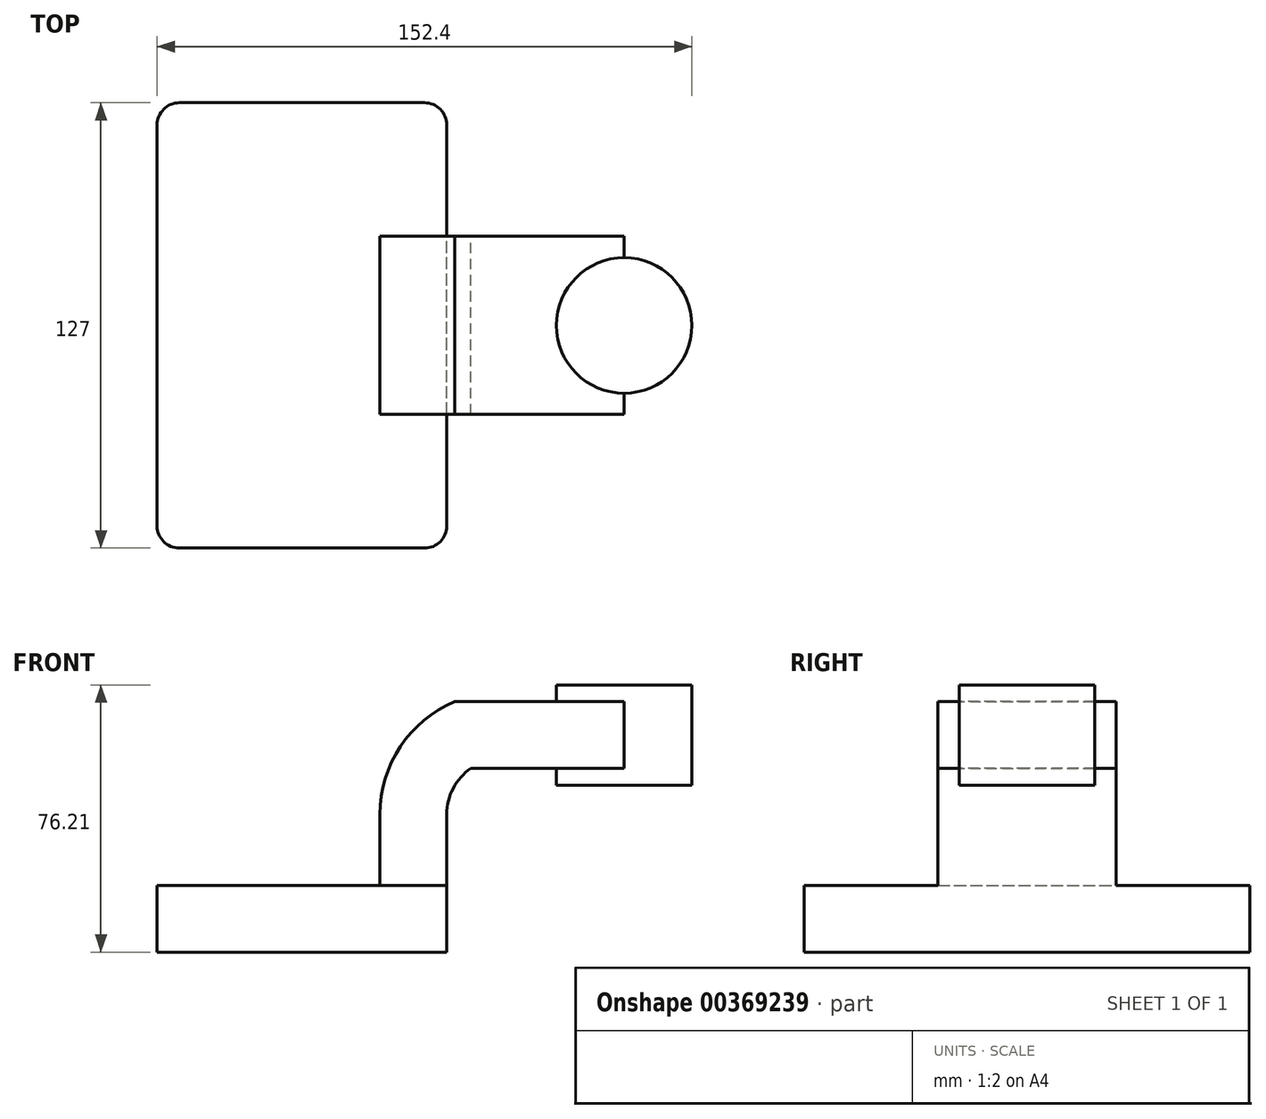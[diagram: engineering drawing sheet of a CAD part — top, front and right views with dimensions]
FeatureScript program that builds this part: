
annotation { "Feature Type Name" : "Feature", "Feature Type Description" : "" }
export const myFeature = defineFeature(function(context is Context, id is Id, definition is map)
    precondition{}
    {
        {
            var Q0;
            Q0=qCreatedBy(makeId("Front.planeOp"),FACE);
            var sketch = newSketch(context, id + "F0", { "sketchPlane" : qUnion([Q0])});
            skLineSegment(sketch, "E0.bottom", {"start": v(41.27, 9.53) * mm, "end": v(-41.28, 9.53) * mm});
            skLineSegment(sketch, "E0.top", {"start": v(41.28, -9.52) * mm, "end": v(-41.27, -9.52) * mm});
            skLineSegment(sketch, "E0.left", {"start": v(41.28, 9.53) * mm, "end": v(41.28, -9.52) * mm});
            skLineSegment(sketch, "E0.right", {"start": v(-41.28, 9.53) * mm, "end": v(-41.27, -9.52) * mm});
            skPoint(sketch, "E0.middle", {"position": v(0, 0) * mm});
            skLineSegment(sketch, "E1.bottom", {"start": v(111.12, 38.1) * mm, "end": v(60.32, 38.1) * mm});
            skLineSegment(sketch, "E1.top", {"start": v(111.12, 66.68) * mm, "end": v(60.32, 66.68) * mm});
            skLineSegment(sketch, "E1.left", {"start": v(111.12, 38.1) * mm, "end": v(111.12, 66.68) * mm});
            skLineSegment(sketch, "E1.right", {"start": v(60.32, 38.1) * mm, "end": v(60.32, 66.68) * mm});
            skPoint(sketch, "E1.middle", {"position": v(85.72, 52.39) * mm});
            skLineSegment(sketch, "E2", {"start": v(41.27, 9.53) * mm, "end": v(41.27, 29.78) * mm});
            skArc(sketch, "E3", {"start": v(41.27, 29.78) * mm, "mid": v(43.1, 37.18) * mm, "end": v(48.17, 42.88) * mm});
            skLineSegment(sketch, "E4", {"start": v(48.17, 42.88) * mm, "end": v(91.81, 42.88) * mm});
            skLineSegment(sketch, "E5.0", {"start": v(43.5, 61.93) * mm, "end": v(91.81, 61.93) * mm});
            skArc(sketch, "E5.1", {"start": v(22.22, 29.78) * mm, "mid": v(28.02, 49.05) * mm, "end": v(43.5, 61.93) * mm});
            skLineSegment(sketch, "E5.2", {"start": v(22.22, 9.53) * mm, "end": v(22.22, 29.78) * mm});
            skLineSegment(sketch, "E6", {"start": v(91.81, 38.1) * mm, "end": v(91.81, 66.68) * mm});
            skFitSpline(sketch, "E7", {"points": [v(-41.28, 9.53) * mm, v(43.5, 61.93) * mm], "startDerivative": vector(1.4, 112.6) * mm, "endDerivative": vector(130.48, 2.8) * mm});
            skSolve(sketch);
        }
        {
            var Q0;
            Q0=makeQuery(id+"F0.imprint","IMPRINT",FACE,{"disambiguationData":[TD([[makeQuery(id+"F0.imprint","IMPRINT",EDGE,{"derivedFrom":sQuery(id+"F0.wireOp",EDGE,"E0.top")}),-1.0]])]});
            extrude(context, id + "F1", {"entities" : qUnion([Q0]), "endBound" : BoundingType.SYMMETRIC, "depth" : 127 * mm});
        }
        {
            var Q0;
            {var subQ1=sQuery(id+"F0.wireOp",EDGE,"E2");Q0=makeQuery(id+"F0.imprint","IMPRINT",FACE,{"disambiguationData":[TD([[makeQuery(id+"F0.imprint","IMPRINT",EDGE,{"derivedFrom":subQ1}),1.0]])]});}
            var Q1;
            {var subQ0=sQuery(id+"F0.wireOp",EDGE,"E4");var subQ1=sQuery(id+"F0.wireOp",EDGE,"E1.right");var subQ2=makeQuery(id+"F0.imprint","INTERSECT",VERTEX,{"derivedFrom":[subQ1,subQ0]});Q1=makeQuery(id+"F0.imprint","IMPRINT",FACE,{"disambiguationData":[TD([[makeQuery(id+"F0.imprint","IMPRINT",EDGE,{"disambiguationData":[TD([[subQ2,-1.0]])],"derivedFrom":subQ1}),-1.0]])]});}
            extrude(context, id + "F2", {"entities" : qUnion([Q0, Q1]), "operationType" : NewBodyOperationType.ADD, "endBound" : BoundingType.SYMMETRIC, "depth" : 50.8 * mm});
        }
        {
            var Q0;
            Q0=makeQuery(id+"F0.imprint","IMPRINT",FACE,{"disambiguationData":[TD([[makeQuery(id+"F0.imprint","IMPRINT",EDGE,{"derivedFrom":sQuery(id+"F0.wireOp",EDGE,"E5.1")}),1.0]])]});
            extrude(context, id + "F3", {"entities" : qUnion([Q0]), "operationType" : NewBodyOperationType.ADD, "endBound" : BoundingType.SYMMETRIC, "depth" : 20.95 * mm});
        }
        {
            var Q0;
            {var subQ4=sQuery(id+"F0.wireOp",EDGE,"E1.left");Q0=makeQuery(id+"F0.imprint","IMPRINT",FACE,{"disambiguationData":[TD([[makeQuery(id+"F0.imprint","IMPRINT",EDGE,{"derivedFrom":subQ4}),1.0]])]});}
            var Q1;
            Q1=sQuery(id+"F0.wireOp",EDGE,"E6");
            var Q2;
            Q2=sQuery(id+"F0.wireOp",EDGE,"E1.right");
            var Q3;
            Q3=sQuery(id+"F0.wireOp",EDGE,"E6");
            revolve(context, id + "F4", {"operationType" : NewBodyOperationType.ADD, "entities" : qUnion([Q0]), "surfaceEntities" : qUnion([Q1, Q2]), "axis" : qUnion([Q3]), "revolveType" : RevolveType.FULL});
        }
        {
            var Q0;
            Q0=makeQuery(id+"F1.opExtrude","CAP_EDGE",EDGE,{"disambiguationData":[OSD([sQuery(id+"F0.wireOp",EDGE,"E0.left")])],"isStart":false});
            var Q1;
            Q1=makeQuery(id+"F1.opExtrude","CAP_EDGE",EDGE,{"disambiguationData":[OSD([sQuery(id+"F0.wireOp",EDGE,"E0.left")])],"isStart":true});
            var Q2;
            Q2=makeQuery(id+"F1.opExtrude","CAP_EDGE",EDGE,{"disambiguationData":[OSD([sQuery(id+"F0.wireOp",EDGE,"E0.right")])],"isStart":true});
            var Q3;
            Q3=makeQuery(id+"F1.opExtrude","CAP_EDGE",EDGE,{"disambiguationData":[OSD([sQuery(id+"F0.wireOp",EDGE,"E0.right")])],"isStart":false});
            fillet(context, id + "F5", {"entities" : qUnion([Q0, Q1, Q2, Q3]), "radius" : 6.35 * mm, "tangentPropagation" : true, "allowEdgeOverflow" : false});
        }
    });
